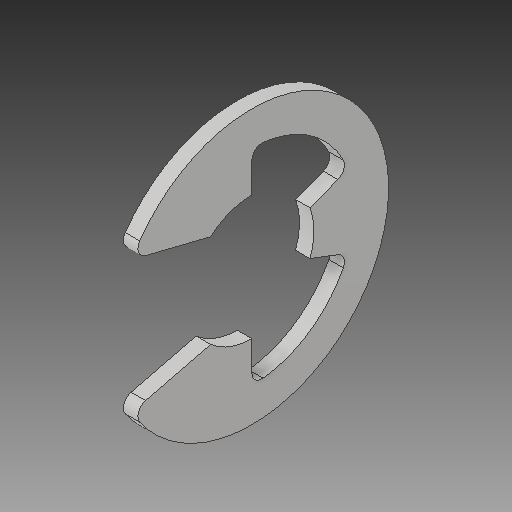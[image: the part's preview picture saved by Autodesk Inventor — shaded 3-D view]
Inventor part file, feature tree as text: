
AUTODESK INVENTOR PART (.ipt)
format: ipt  version: 2017 (Build 210142000, 142)  size: 109,568 bytes
history: native  units: in
note: dims shown in document units (in); Inventor stores cm internally (conversion verified against a paired STEP export)
features: fillet x1
ambient origin geometry x8: Origin, YZ Plane, XZ Plane, XY Plane, X Axis, Y Axis, Z Axis, Center Point
bodies: Solid1 (feature_tree)
feature tree (1):
  fillet  "Fillet1"  [1 undecoded]
note: 1 required parameter value undecoded (feature->parameter linkage not recoverable at this tier; creation-order binding heuristic only, values carry confidence <= 0.55)
